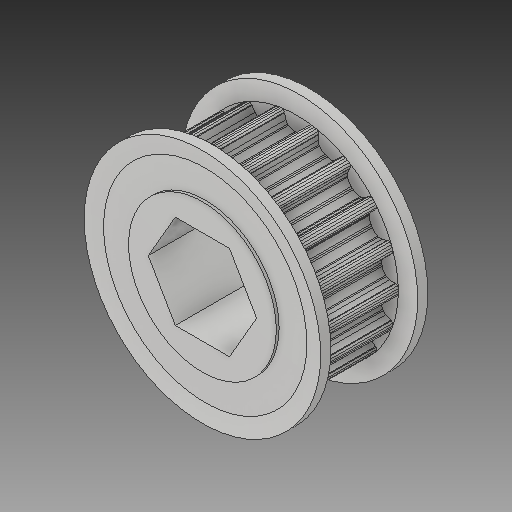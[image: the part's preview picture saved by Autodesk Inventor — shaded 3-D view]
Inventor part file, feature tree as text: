
AUTODESK INVENTOR PART (.ipt)
format: ipt  version: 2018 (Build 220112000, 112)  size: 545,280 bytes
history: native  units: in
note: dims shown in document units (in); Inventor stores cm internally (conversion verified against a paired STEP export)
features: mirror x1
ambient origin geometry x8: Origin, YZ Plane, XZ Plane, XY Plane, X Axis, Y Axis, Z Axis, Center Point
bodies: Solid1 (feature_tree)
feature tree (1):
  mirror  "Mirror1"
